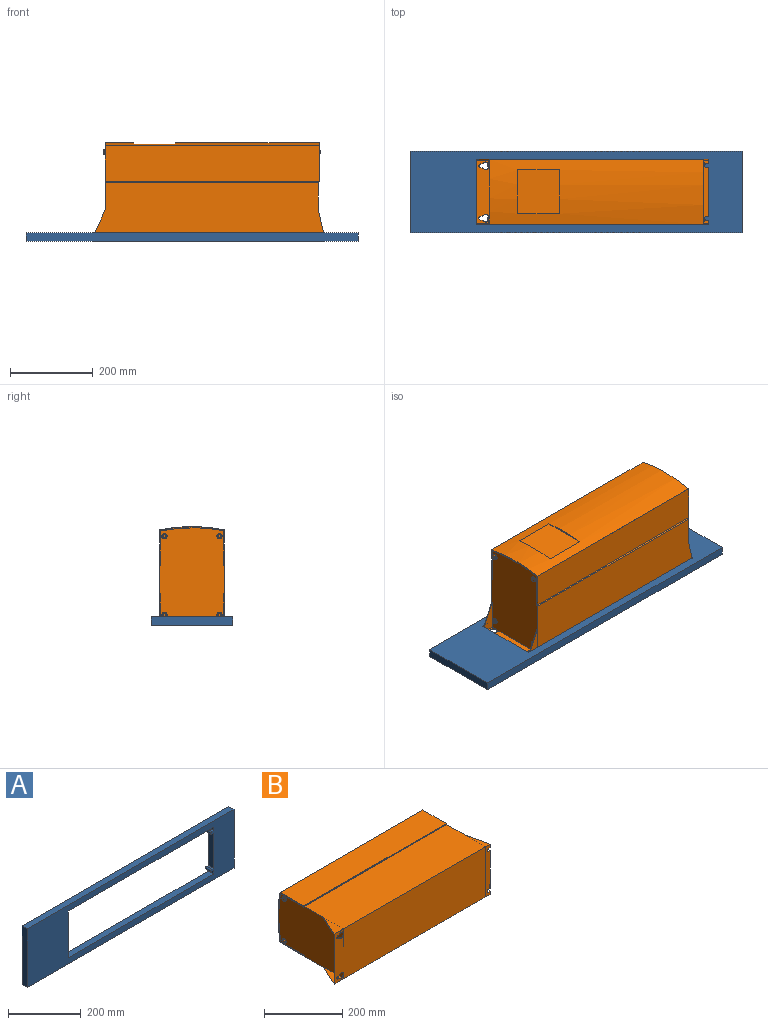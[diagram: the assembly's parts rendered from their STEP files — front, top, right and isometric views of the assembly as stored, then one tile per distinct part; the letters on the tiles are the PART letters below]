
ASSEMBLY  parts=2 mates=1
PART A: 18 faces, bbox 802x20x197 mm
  f0: plane 157x20mm, normal (1,0,0), area 3140mm2, adj f1,f15,f16,f17
  f1: plane 562x20mm, normal (0,0,-1), area 11240mm2, adj f0,f2,f16,f17
  f2: plane 20x10.5mm, normal (-1,0,0), area 210mm2, adj f1,f3,f16,f17
  f3: plane 20x6mm, normal (0,0,1), area 120mm2, adj f2,f4,f16,f17
  f4: extruded ~20x9mm, area 282.7mm2, adj f3,f5,f16,f17
  f5: plane 20x6mm, normal (0,0,-1), area 120mm2, adj f4,f6,f16,f17
  f6: plane 118x20mm, normal (-1,0,0), area 2360mm2, adj f5,f7,f16,f17
  f7: plane 20x6mm, normal (0,0,1), area 120mm2, adj f6,f8,f16,f17
  f8: extruded ~20x9mm, area 282.7mm2, adj f7,f9,f16,f17
  f9: plane 20x6mm, normal (0,0,-1), area 120mm2, adj f8,f10,f16,f17
  f10: plane 20x10.5mm, normal (-1,0,0), area 210mm2, adj f9,f15,f16,f17
  f11: plane 802x20mm, normal (0,0,1), area 16040mm2, adj f12,f14,f16,f17
  f12: plane 197x20mm, normal (-1,0,0), area 3940mm2, adj f11,f13,f16,f17
  f13: plane 802x20mm, normal (0,0,-1), area 16040mm2, adj f12,f14,f16,f17
  f14: plane 197x20mm, normal (1,0,0), area 3940mm2, adj f11,f13,f16,f17
  f15: plane 562x20mm, normal (0,0,1), area 11240mm2, adj f0,f10,f16,f17
  f16: plane 802x197mm, normal (0,1,0), area 69931.4mm2, adj f0,f1,f2,f3,f4,f5,f6,f7
  f17: plane 802x197mm, normal (0,-1,0), area 69931.4mm2, adj f0,f1,f2,f3,f4,f5,f6,f7
PART B: 78 faces, bbox 562x238x157 mm
  f0: plane 105.6x3.5mm, normal (1,0,0), area 246.6mm2, adj f2,f11
  f1: plane 105.6x3.5mm, normal (-1,0,0), area 246.6mm2, adj f2,f11
  f2: plane 105.6x101mm, normal (0,1,0), area 10665.4mm2, adj f0,f1,f11
  f3: plane 7.62x7.62mm, normal (1,0,0), area 45.6mm2, adj f16
  f4: plane 7.62x7.62mm, normal (1,0,0), area 45.6mm2, adj f17
  f5: plane 7.62x7.62mm, normal (1,0,0), area 45.6mm2, adj f18
  f6: plane 7.62x7.62mm, normal (1,0,0), area 45.6mm2, adj f19
  f7: plane 517.51x2.54mm, normal (0,-1,0), area 1314.5mm2, adj f9,f20,f21,f23
  f8: plane 517.51x2.54mm, normal (0,-1,0), area 1314.5mm2, adj f10,f21,f22,f23
  f9: plane 517.51x85.22mm, normal (0,0,-1), area 44103.4mm2, adj f7,f11,f21,f23
  f10: plane 517.51x85.22mm, normal (0,0,1), area 44103.4mm2, adj f8,f11,f21,f23
  f11: cylinder r=400mm len=517.51mm, axis (1,0,0), area 71083.9mm2, adj f0,f1,f2,f9,f10,f21,f23
  f12: plane 7.62x7.62mm, normal (-1,0,0), area 45.6mm2, adj f24
  f13: plane 7.62x7.62mm, normal (-1,0,0), area 45.6mm2, adj f25
  f14: plane 7.62x7.62mm, normal (-1,0,0), area 45.6mm2, adj f26
  f15: plane 7.62x7.62mm, normal (-1,0,0), area 45.6mm2, adj f27
  f16: torus R=3.81mm, axis (1,0,0), area 136mm2, adj f3,f29
  f17: torus R=3.81mm, axis (1,0,0), area 136mm2, adj f4,f30
  f18: torus R=3.81mm, axis (1,0,0), area 136mm2, adj f5,f31
  f19: torus R=3.81mm, axis (1,0,0), area 136mm2, adj f6,f32
  f20: plane 517.51x83.13mm, normal (0,0,1), area 43023.1mm2, adj f7,f21,f23,f34
  f21: plane 157.01x93.01mm, normal (-1,0,0), area 822.5mm2, adj f7,f8,f9,f10,f11,f20,f22,f34
  f22: plane 517.51x83.13mm, normal (0,0,-1), area 43023.1mm2, adj f8,f21,f23,f34
  f23: plane 157.01x93.01mm, normal (1,0,0), area 822.4mm2, adj f7,f8,f9,f10,f11,f20,f22,f34
  f24: torus R=3.81mm, axis (1,0,0), area 136mm2, adj f12,f36
  f25: torus R=3.81mm, axis (1,0,0), area 136mm2, adj f13,f37
  f26: torus R=3.81mm, axis (1,0,0), area 136mm2, adj f14,f38
  f27: torus R=3.81mm, axis (1,0,0), area 136mm2, adj f15,f39
  f28: cylinder r=1.27mm len=515mm, axis (1,0,0), area 812.1mm2, adj f33,f45,f49,f52
  f29: cylinder r=6.35mm len=12.7mm, axis (1,0,0), area 50.7mm2, adj f16,f49
  f30: cylinder r=6.35mm len=12.7mm, axis (1,0,0), area 50.7mm2, adj f17,f49
  f31: cylinder r=6.35mm len=12.7mm, axis (1,0,0), area 50.7mm2, adj f18,f49
  f32: cylinder r=6.35mm len=12.7mm, axis (1,0,0), area 50.7mm2, adj f19,f49
  f33: plane 515x83.43mm, normal (0,0,-1), area 42968.5mm2, adj f28,f34,f49,f52
  f34: cylinder r=397.46mm len=517.51mm, axis (1,0,0), area 1183.8mm2, adj f20,f21,f22,f23,f33,f35,f49,f52
  f35: plane 515x83.43mm, normal (0,0,1), area 42968.5mm2, adj f34,f40,f49,f52
  f36: cylinder r=6.35mm len=12.7mm, axis (1,0,0), area 50.7mm2, adj f24,f52
  f37: cylinder r=6.35mm len=12.7mm, axis (1,0,0), area 50.7mm2, adj f25,f52
  f38: cylinder r=6.35mm len=12.7mm, axis (1,0,0), area 50.7mm2, adj f26,f52
  f39: cylinder r=6.35mm len=12.7mm, axis (1,0,0), area 50.7mm2, adj f27,f52
  f40: cylinder r=1.27mm len=515mm, axis (1,0,0), area 812.1mm2, adj f35,f49,f52,f53
  f41: plane 73.22x15.5mm, normal (0,0,-1), area 606.2mm2, adj f42,f49,f50,f57
  f42: plane 154x15.5mm, normal (0,1,0), area 2215.4mm2, adj f41,f43,f49,f57,f58,f59,f60,f61
  f43: plane 73.22x15.5mm, normal (0,0,1), area 606.2mm2, adj f42,f44,f49,f65
  f44: plane 68.22x15.5mm, normal (0.98,0.22,0), area 104.9mm2, adj f43,f49,f65,f66
  f45: cylinder r=3.94mm len=515mm, axis (1,0,0), area 1833.1mm2, adj f28,f49,f52,f66
  f46: plane 69.44x31.5mm, normal (-0.91,0.41,0), area 114.4mm2, adj f47,f52,f66,f67
  f47: plane 74.44x31.5mm, normal (0,0,1), area 1251.2mm2, adj f46,f52,f56,f67
  f48: plane 74.44x31.5mm, normal (0,0,-1), area 1251.2mm2, adj f51,f52,f56,f67
  f49: plane 233.97x157.01mm, normal (1,0,0), area 35036.3mm2, adj f28,f29,f30,f31,f32,f33,f34,f35
  f50: plane 68.22x15.5mm, normal (0.98,0.22,0), area 104.9mm2, adj f41,f49,f57,f68
  f51: plane 69.44x31.5mm, normal (-0.91,0.41,0), area 114.4mm2, adj f48,f52,f67,f68
  f52: plane 233.97x157.01mm, normal (-1,0,0), area 35033.2mm2, adj f28,f33,f34,f35,f36,f37,f38,f39
  f53: cylinder r=3.94mm len=515mm, axis (1,0,0), area 1833.1mm2, adj f40,f49,f52,f68
  f54: plane 5.92x0.5mm, normal (0,-1,0), area 2mm2, adj f52,f69
  f55: plane 5.92x0.5mm, normal (0,-1,0), area 2mm2, adj f52,f75
  f56: plane 154x31.5mm, normal (0,1,0), area 4221.4mm2, adj f47,f48,f52,f67,f69,f70,f71,f72
  f57: plane 10.5x6.5mm, normal (1,0,0), area 23.2mm2, adj f41,f42,f50,f58,f68,f77
  f58: plane 6x1.5mm, normal (0,0,-1), area 9mm2, adj f42,f57,f59,f77
  f59: cylinder r=4.5mm len=9mm, axis (0,1,0), area 21.2mm2, adj f42,f58,f60,f77
  f60: plane 6x1.5mm, normal (0,0,1), area 9mm2, adj f42,f59,f61,f77
  f61: plane 118x1.5mm, normal (1,0,0), area 177mm2, adj f42,f60,f62,f77
  f62: plane 6x1.5mm, normal (0,0,-1), area 9mm2, adj f42,f61,f63,f77
  f63: cylinder r=4.5mm len=9mm, axis (0,1,0), area 21.2mm2, adj f42,f62,f64,f77
  f64: plane 6x1.5mm, normal (0,0,1), area 9mm2, adj f42,f63,f65,f77
  f65: plane 10.5x6.5mm, normal (1,0,0), area 23.2mm2, adj f42,f43,f44,f64,f66,f77
  f66: plane 562x141.22mm, normal (0,0,-1), area 74658.3mm2, adj f44,f45,f46,f49,f52,f65,f67,f77
  f67: plane 157x6.5mm, normal (-1,0,0), area 250.5mm2, adj f46,f47,f48,f51,f56,f66,f68,f77
  f68: plane 562x141.22mm, normal (0,0,1), area 74658.3mm2, adj f49,f50,f51,f52,f53,f57,f67,f77
  f69: cylinder r=9mm len=18mm, axis (0,1,0), area 70.7mm2, adj f54,f56,f70,f72,f77
  f70: plane 4.21x1.5mm, normal (0,0,-1), area 6.3mm2, adj f56,f69,f71,f77
  f71: cylinder r=4.5mm len=9mm, axis (0,1,0), area 21.2mm2, adj f56,f70,f72,f77
  f72: plane 4.21x1.5mm, normal (0,0,1), area 6.3mm2, adj f56,f69,f71,f77
  f73: cylinder r=4.5mm len=9mm, axis (0,1,0), area 21.2mm2, adj f56,f74,f76,f77
  f74: plane 4.21x1.5mm, normal (0,0,1), area 6.3mm2, adj f56,f73,f75,f77
  f75: cylinder r=9mm len=18mm, axis (0,1,0), area 70.7mm2, adj f55,f56,f74,f76,f77
  f76: plane 4.21x1.5mm, normal (0,0,-1), area 6.3mm2, adj f56,f73,f75,f77
  f77: plane 562.01x157.01mm, normal (0,-1,0), area 87428.5mm2, adj f57,f58,f59,f60,f61,f62,f63,f64
PLACE A rot(axis=(1,0,0),90deg) t=(0,0.81,-19.33)mm
PLACE B rot(axis=(1,0,0),90deg) t=(0,0.81,-19.33)mm
MATE fastened B.f77 <-> A.f17  axis (0,0,-1) through (-281,-77.69,-19.33)mm
